# Revit family: Sun 190807
name_source: partatom
category: Furniture
units: mm (PartAtom-declared; Revit-internal decimal feet)

## family parameters
Always vertical = Yes
Cut with Voids When Loaded = No
OmniClass Number = 23.40.20.00
OmniClass Title = General Furniture and Specialties
Room Calculation Point = No
Shared = No
Work Plane-Based = No

## types (24) — shared parameters
Body Material = Moisture resistant chipboard E1 and FSC certified.
Front Material = Moiusture resistant MDF E1 and FSC certified
Manufacturer = Hafa Bathroom Group AB
Model = New Sun (2018)
Svulsthöjd = 752 mm

## per-type parameters (varying)
| type | Article number | Depth | Finish | GTIN | Handtag integrerade | Type Comments | URL | Width |
| Sun 600 white matt | 1390100 | 439 mm  [stored 1.44029 ft] | White matt NCS S 0300-N 20% gloss | 7330027109282 | 250 mm  [stored 0.82021 ft] |  | https://www.hafa.se | 600 mm |
| Sun 800 white matt | 1390105 | 439 mm  [stored 1.44029 ft] | White matt NCS S 0300-N 20% gloss | 7330027109329 | 350 mm  [stored 1.14829 ft] |  | https://www.hafa.se | 800 mm  [stored 2.62467 ft] |
| Sun 900 white matt | 1390100 | 439 mm  [stored 1.44029 ft] | White matt NCS S 0300-N 20% gloss | 7330027109282 | 400 mm  [stored 1.31234 ft] |  | https://www.hafa.se | 900 mm  [stored 2.95276 ft] |
| Sun 1000 white matt | 1390115 | 439 mm  [stored 1.44029 ft] | White matt NCS S 0300-N 20% gloss | 7330027109404 | 430 mm |  | www.hafa.se | 1000 mm  [stored 3.28084 ft] |
| Sun compact 600 white matt | 1390220 | 369 mm | White matt NCS S 0300-N 20% gloss | 7330027109640 | 250 mm  [stored 0.82021 ft] | www.hafa.se |  | 600 mm |
| Sun compact 800 white matt | 1390229 | 369 mm | White matt NCS S 0300-N 20% gloss | 7330027109732 | 350 mm  [stored 1.14829 ft] |  | www.hafa.se | 800 mm  [stored 2.62467 ft] |
| Sun 600 grey matt | 1390103 | 439 mm  [stored 1.44029 ft] | Grey matt NCS S 4500-N 10% gloss | 7330027109305 | 250 mm  [stored 0.82021 ft] |  | https://www.hafa.se | 600 mm |
| Sun 600 anthracite | 1390101 | 439 mm  [stored 1.44029 ft] | Anthracite NCS S 8000-N 10% gloss | 7330027109299 | 250 mm  [stored 0.82021 ft] |  | https://www.hafa.se | 600 mm |
| Sun 600 ash foil | 1390104 | 439 mm  [stored 1.44029 ft] | Ash foil | 7330027109312 | 250 mm  [stored 0.82021 ft] |  | https://www.hafa.se | 600 mm |
| Sun 800 grey matt | 1390108 | 439 mm  [stored 1.44029 ft] | Grey matt NCS S 4500-N 10% gloss | 7330027109343 | 350 mm  [stored 1.14829 ft] |  | https://www.hafa.se | 800 mm  [stored 2.62467 ft] |
| Sun 800 anthracite matt | 1390106 | 439 mm  [stored 1.44029 ft] | NCS S 8000-N 10% gloss | 7330027109336 | 350 mm  [stored 1.14829 ft] |  | https://www.hafa.se | 800 mm  [stored 2.62467 ft] |
| Sun 800 ash foil | 1390109 | 439 mm  [stored 1.44029 ft] | Ash foil | 7330027109350 | 350 mm  [stored 1.14829 ft] |  | https://www.hafa.se | 800 mm  [stored 2.62467 ft] |
| Sun 900 grey matt | 1390103 | 439 mm  [stored 1.44029 ft] | Grey matt NCS S 4500-N 10% gloss | 7330027109305 | 400 mm  [stored 1.31234 ft] |  | https://www.hafa.se | 900 mm  [stored 2.95276 ft] |
| Sun 900 ash foil | 1390104 | 439 mm  [stored 1.44029 ft] | Ash foil | 7330027109312 | 400 mm  [stored 1.31234 ft] |  | https://www.hafa.se | 900 mm  [stored 2.95276 ft] |
| Sun 900 anthracite matt | 1390101 | 439 mm  [stored 1.44029 ft] | Anthracite NCS S 8000-N 10% gloss | 7330027109299 | 400 mm  [stored 1.31234 ft] |  | https://www.hafa.se | 900 mm  [stored 2.95276 ft] |
| Sun 1000 anthractie matt | 1390116 | 439 mm  [stored 1.44029 ft] | Anthracite NCS S 8000-N 10% gloss | 7330027109411 | 430 mm |  | www.hafa.se | 1000 mm  [stored 3.28084 ft] |
| Sun 1000 ash foil | 1390119 | 439 mm  [stored 1.44029 ft] | Ash foil | 733002710943 | 430 mm |  | www.hafa.se | 1000 mm  [stored 3.28084 ft] |
| Sun 1000 grey matt | 1390118 | 439 mm  [stored 1.44029 ft] | Grey matt NCS S 4500-N 10% gloss | 7330027109428 | 430 mm |  | www.hafa.se | 1000 mm  [stored 3.28084 ft] |
| Sun compact 600 antrhactie matt | 1390221 | 369 mm | Anthracite NCS S 8000-N 10% gloss | 7330027109657 | 250 mm  [stored 0.82021 ft] | www.hafa.se |  | 600 mm |
| Sun compact 600 grey matt | 1390222 | 369 mm | Grey matt NCS S 4500-N 10% gloss | 7330027109664 | 250 mm  [stored 0.82021 ft] | www.hafa.se |  | 600 mm |
| Sun compact 600 ash foil | 1390223 | 369 mm | Ash foil | 7330027109671 | 250 mm  [stored 0.82021 ft] | www.hafa.se |  | 600 mm |
| Sun compact 800 grey matt | 1390231 | 369 mm | Grey matt NCS S 4500-N 10% gloss | 7330027109756 | 350 mm  [stored 1.14829 ft] |  | www.hafa.se | 800 mm  [stored 2.62467 ft] |
| Sun compact 800 ash foil | 1390232 | 369 mm | Ash foil | 7330027109763 | 350 mm  [stored 1.14829 ft] |  | www.hafa.se | 800 mm  [stored 2.62467 ft] |
| Sun compact 800 anthracite matt | 1390230 | 369 mm | Anthracite NCS S 8000-N 10% gloss | 7330027109749 | 350 mm  [stored 1.14829 ft] |  | www.hafa.se | 800 mm  [stored 2.62467 ft] |

note: [stored X ft] marks values corroborated as IEEE doubles in the binary element streams (Revit-internal decimal feet)

## geometry (parser evidence)
native form markers: Sweep x3
no freeform markers — native parametric forms only
